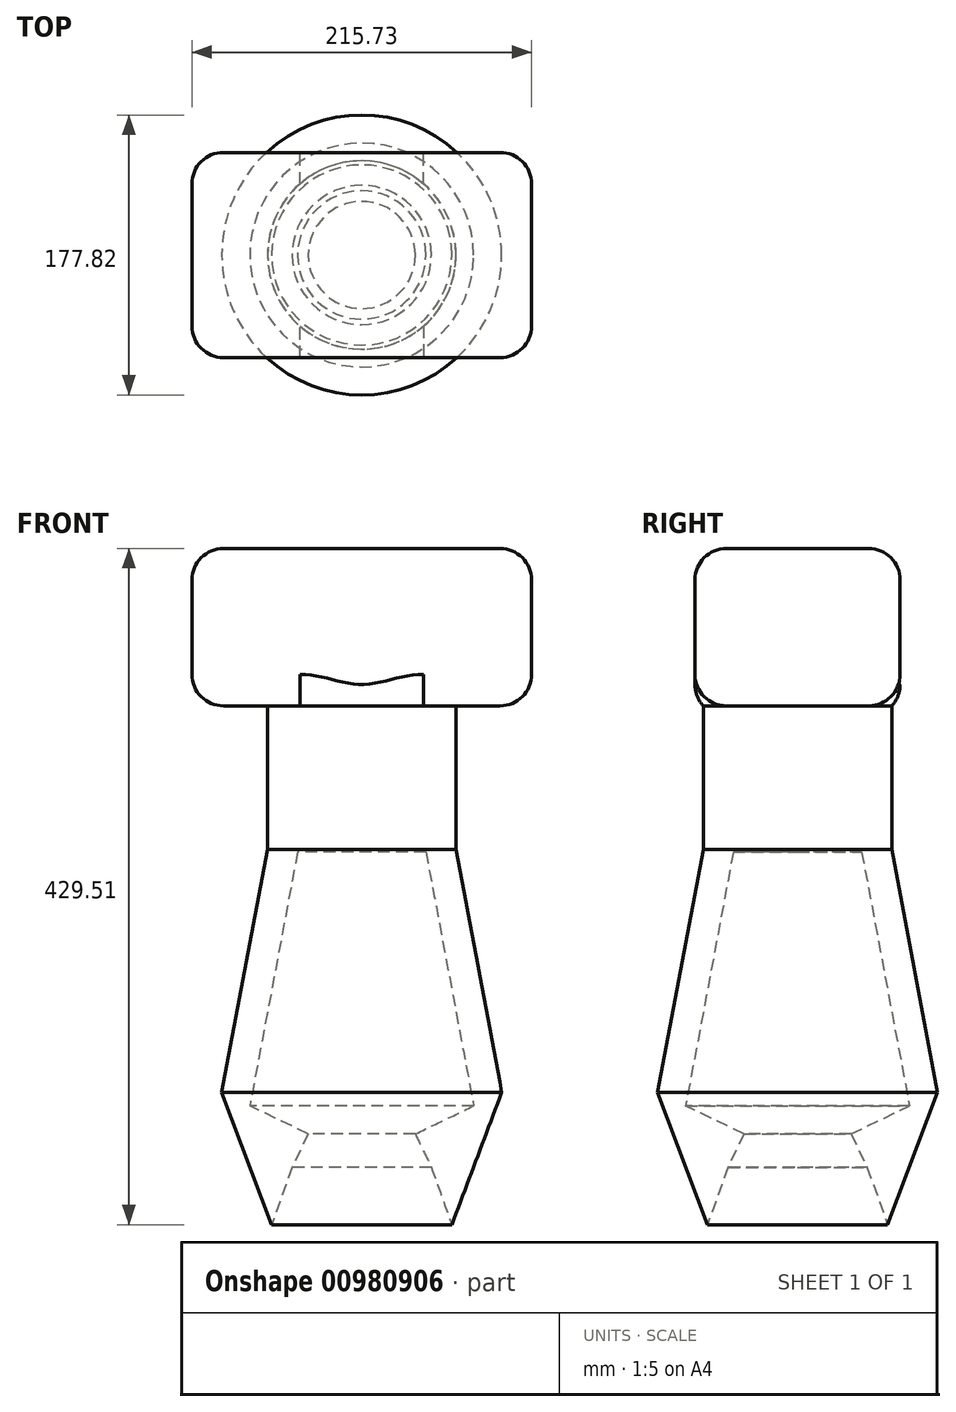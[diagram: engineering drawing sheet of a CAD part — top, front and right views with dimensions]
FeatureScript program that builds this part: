
annotation { "Feature Type Name" : "Feature", "Feature Type Description" : "" }
export const myFeature = defineFeature(function(context is Context, id is Id, definition is map)
    precondition{}
    {
        {
            var Q0;
            Q0=qCreatedBy(makeId("Front.planeOp"),FACE);
            var sketch = newSketch(context, id + "F0", { "sketchPlane" : qUnion([Q0])});
            skLineSegment(sketch, "E0", {"start": v(-398.48, 108.19) * mm, "end": v(-398.48, -266.65) * mm});
            skLineSegment(sketch, "E1.bottom", {"start": v(-312.62, 21.55) * mm, "end": v(-484.34, 21.55) * mm});
            skLineSegment(sketch, "E1.top", {"start": v(-312.62, 194.83) * mm, "end": v(-484.34, 194.83) * mm});
            skLineSegment(sketch, "E1.left", {"start": v(-312.62, 21.55) * mm, "end": v(-312.62, 194.83) * mm});
            skLineSegment(sketch, "E1.right", {"start": v(-484.34, 21.55) * mm, "end": v(-484.34, 194.83) * mm});
            skPoint(sketch, "E1.middle", {"position": v(-398.48, 108.19) * mm});
            skLineSegment(sketch, "E2", {"start": v(-439.22, 21.55) * mm, "end": v(-439.22, -71.24) * mm});
            skLineSegment(sketch, "E3", {"start": v(-439.22, -71.24) * mm, "end": v(-398.48, -71.24) * mm});
            skPoint(sketch, "E3.endSnap0", {"position": v(-398.48, -79.23) * mm});
            skLineSegment(sketch, "E4", {"start": v(-439.22, -71.24) * mm, "end": v(-469.57, -232.52) * mm});
            skLineSegment(sketch, "E5", {"start": v(-469.57, -232.52) * mm, "end": v(-398.48, -266.65) * mm});
            skLineSegment(sketch, "E6.MirrorCS", {"start": v(-357.74, 21.55) * mm, "end": v(-357.74, -71.24) * mm});
            skLineSegment(sketch, "E7.MirrorCS", {"start": v(-357.74, -71.24) * mm, "end": v(-398.48, -71.24) * mm});
            skLineSegment(sketch, "E8.MirrorCS", {"start": v(-357.74, -71.24) * mm, "end": v(-327.4, -232.52) * mm});
            skLineSegment(sketch, "E9.MirrorCS", {"start": v(-327.4, -232.52) * mm, "end": v(-398.48, -266.65) * mm});
            skLineSegment(sketch, "E10", {"start": v(-458.3, 21.55) * mm, "end": v(-458.3, -69.5) * mm});
            skLineSegment(sketch, "E11", {"start": v(-458.3, -69.5) * mm, "end": v(-487.4, -224.1) * mm});
            skLineSegment(sketch, "E12", {"start": v(-487.4, -224.1) * mm, "end": v(-455.7, -307.96) * mm});
            skLineSegment(sketch, "E13", {"start": v(-455.7, -307.96) * mm, "end": v(-442.7, -271.54) * mm});
            skLineSegment(sketch, "E14", {"start": v(-442.7, -271.54) * mm, "end": v(-432.5, -250.32) * mm});
            skLineSegment(sketch, "E15.MirrorCS", {"start": v(-338.67, -69.5) * mm, "end": v(-309.58, -224.1) * mm});
            skLineSegment(sketch, "E16.MirrorCS", {"start": v(-338.67, 21.55) * mm, "end": v(-338.67, -69.5) * mm});
            skLineSegment(sketch, "E17.MirrorCS", {"start": v(-309.58, -224.1) * mm, "end": v(-341.27, -307.96) * mm});
            skLineSegment(sketch, "E18.MirrorCS", {"start": v(-341.27, -307.96) * mm, "end": v(-354.27, -271.54) * mm});
            skLineSegment(sketch, "E19.MirrorCS", {"start": v(-354.27, -271.54) * mm, "end": v(-364.46, -250.32) * mm});
            skSolve(sketch);
        }
        {
            var Q0;
            {var subQ4=sQuery(id+"F0.wireOp",EDGE,"E2");Q0=makeQuery(id+"F0.imprint","IMPRINT",FACE,{"disambiguationData":[TD([[makeQuery(id+"F0.imprint","IMPRINT",EDGE,{"derivedFrom":subQ4}),1.0]])]});}
            var Q1;
            {var subQ3=sQuery(id+"F0.wireOp",EDGE,"E2");Q1=makeQuery(id+"F0.imprint","IMPRINT",FACE,{"disambiguationData":[TD([[makeQuery(id+"F0.imprint","IMPRINT",EDGE,{"derivedFrom":subQ3}),-1.0]])]});}
            var Q2;
            Q2=sQuery(id+"F0.wireOp",EDGE,"E0");
            revolve(context, id + "F1", {"surfaceOperationType" : NewSurfaceOperationType.NEW, "entities" : qUnion([Q0, Q1]), "axis" : qUnion([Q2]), "revolveType" : RevolveType.FULL});
        }
        {
            var Q0;
            Q0=makeQuery(id+"F1.opRevolve","SWEPT_FACE",FACE,{"disambiguationData":[OSD([sQuery(id+"F0.wireOp",EDGE,"E1.bottom")])]});
            var sketch = newSketch(context, id + "F2", { "sketchPlane" : qUnion([Q0])});
            skLineSegment(sketch, "E20.bottom", {"start": v(-290.62, -65.15) * mm, "end": v(-506.35, -65.15) * mm});
            skLineSegment(sketch, "E20.top", {"start": v(-290.62, 65.15) * mm, "end": v(-506.35, 65.15) * mm});
            skLineSegment(sketch, "E20.left", {"start": v(-290.62, -65.15) * mm, "end": v(-290.62, 65.15) * mm});
            skLineSegment(sketch, "E20.right", {"start": v(-506.35, -65.15) * mm, "end": v(-506.35, 65.15) * mm});
            skPoint(sketch, "E20.middle", {"position": v(-398.48, 0) * mm});
            skLineSegment(sketch, "E21", {"start": v(-454.64, 65.15) * mm, "end": v(-454.64, -65.15) * mm});
            skLineSegment(sketch, "E22", {"start": v(-398.48, 65.15) * mm, "end": v(-398.48, -65.15) * mm});
            skLineSegment(sketch, "E23.MirrorCS", {"start": v(-342.33, 65.15) * mm, "end": v(-342.33, -65.15) * mm});
            skSolve(sketch);
        }
        {
            var Q0;
            {var subQ0=sQuery(id+"F2.wireOp",EDGE,"E21");var subQ1=makeQuery(id+"F1.opRevolve","SWEPT_EDGE",EDGE,{"disambiguationData":[OSD([sQuery(id+"F0.wireOp",EDGE,"E1.bottom"),sQuery(id+"F0.wireOp",EDGE,"E10")])]});var subQ2=makeQuery(id+"F2.imprint","INTERSECT",VERTEX,{"disambiguationData":[OD(0.0)],"derivedFrom":[subQ1,subQ0]});Q0=makeQuery(id+"F2.imprint","IMPRINT",FACE,{"disambiguationData":[TD([[makeQuery(id+"F2.imprint","IMPRINT",EDGE,{"disambiguationData":[TD([[subQ2,-1.0]])],"derivedFrom":subQ0}),-1.0]])]});}
            var Q1;
            {var subQ0=sQuery(id+"F2.wireOp",EDGE,"E23.MirrorCS");var subQ1=makeQuery(id+"F1.opRevolve","SWEPT_EDGE",EDGE,{"disambiguationData":[OSD([sQuery(id+"F0.wireOp",EDGE,"E1.bottom"),sQuery(id+"F0.wireOp",EDGE,"E10")])]});var subQ2=makeQuery(id+"F2.imprint","INTERSECT",VERTEX,{"disambiguationData":[OD(0.0)],"derivedFrom":[subQ1,subQ0]});Q1=makeQuery(id+"F2.imprint","IMPRINT",FACE,{"disambiguationData":[TD([[makeQuery(id+"F2.imprint","IMPRINT",EDGE,{"disambiguationData":[TD([[subQ2,-1.0]])],"derivedFrom":subQ0}),1.0]])]});}
            var Q2;
            {var subQ5=sQuery(id+"F2.wireOp",EDGE,"E20.left");Q2=makeQuery(id+"F2.imprint","IMPRINT",FACE,{"disambiguationData":[TD([[makeQuery(id+"F2.imprint","IMPRINT",EDGE,{"derivedFrom":subQ5}),1.0]])]});}
            var Q3;
            {var subQ0=sQuery(id+"F2.wireOp",EDGE,"E22");var subQ1=makeQuery(id+"F1.opRevolve","SWEPT_EDGE",EDGE,{"disambiguationData":[OSD([sQuery(id+"F0.wireOp",EDGE,"E1.bottom"),sQuery(id+"F0.wireOp",EDGE,"E10")])]});var subQ2=makeQuery(id+"F2.imprint","INTERSECT",VERTEX,{"disambiguationData":[OD(0.0)],"derivedFrom":[subQ1,subQ0]});Q3=makeQuery(id+"F2.imprint","IMPRINT",FACE,{"disambiguationData":[TD([[makeQuery(id+"F2.imprint","IMPRINT",EDGE,{"disambiguationData":[TD([[subQ2,-1.0]])],"derivedFrom":subQ0}),1.0]])]});}
            var Q4;
            {var subQ0=sQuery(id+"F2.wireOp",EDGE,"E22");var subQ1=sQuery(id+"F2.wireOp",EDGE,"E20.top");var subQ2=makeQuery(id+"F2.imprint","INTERSECT",VERTEX,{"derivedFrom":[subQ1,subQ0]});Q4=makeQuery(id+"F2.imprint","IMPRINT",FACE,{"disambiguationData":[TD([[makeQuery(id+"F2.imprint","IMPRINT",EDGE,{"disambiguationData":[TD([[subQ2,1.0]])],"derivedFrom":subQ1}),1.0]])]});}
            var Q5;
            {var subQ0=sQuery(id+"F2.wireOp",EDGE,"E22");var subQ1=sQuery(id+"F2.wireOp",EDGE,"E20.bottom");var subQ2=makeQuery(id+"F2.imprint","INTERSECT",VERTEX,{"derivedFrom":[subQ1,subQ0]});Q5=makeQuery(id+"F2.imprint","IMPRINT",FACE,{"disambiguationData":[TD([[makeQuery(id+"F2.imprint","IMPRINT",EDGE,{"disambiguationData":[TD([[subQ2,1.0]])],"derivedFrom":subQ1}),-1.0]])]});}
            var Q6;
            {var subQ0=sQuery(id+"F2.wireOp",EDGE,"E21");var subQ1=sQuery(id+"F2.wireOp",EDGE,"E20.bottom");var subQ2=makeQuery(id+"F2.imprint","INTERSECT",VERTEX,{"derivedFrom":[subQ1,subQ0]});Q6=makeQuery(id+"F2.imprint","IMPRINT",FACE,{"disambiguationData":[TD([[makeQuery(id+"F2.imprint","IMPRINT",EDGE,{"disambiguationData":[TD([[subQ2,1.0]])],"derivedFrom":subQ1}),-1.0]])]});}
            var Q7;
            {var subQ5=sQuery(id+"F2.wireOp",EDGE,"E20.right");Q7=makeQuery(id+"F2.imprint","IMPRINT",FACE,{"disambiguationData":[TD([[makeQuery(id+"F2.imprint","IMPRINT",EDGE,{"derivedFrom":subQ5}),-1.0]])]});}
            var Q8;
            {var subQ0=sQuery(id+"F2.wireOp",EDGE,"E21");var subQ1=sQuery(id+"F2.wireOp",EDGE,"E20.top");var subQ2=makeQuery(id+"F2.imprint","INTERSECT",VERTEX,{"derivedFrom":[subQ1,subQ0]});Q8=makeQuery(id+"F2.imprint","IMPRINT",FACE,{"disambiguationData":[TD([[makeQuery(id+"F2.imprint","IMPRINT",EDGE,{"disambiguationData":[TD([[subQ2,1.0]])],"derivedFrom":subQ1}),1.0]])]});}
            var Q9;
            {var subQ0=sQuery(id+"F2.wireOp",EDGE,"E21");var subQ1=makeQuery(id+"F1.opRevolve","SWEPT_EDGE",EDGE,{"disambiguationData":[OSD([sQuery(id+"F0.wireOp",EDGE,"E1.bottom"),sQuery(id+"F0.wireOp",EDGE,"E10")])]});var subQ2=makeQuery(id+"F2.imprint","INTERSECT",VERTEX,{"disambiguationData":[OD(0.0)],"derivedFrom":[subQ1,subQ0]});Q9=makeQuery(id+"F2.imprint","IMPRINT",FACE,{"disambiguationData":[TD([[makeQuery(id+"F2.imprint","IMPRINT",EDGE,{"disambiguationData":[TD([[subQ2,-1.0]])],"derivedFrom":subQ0}),1.0]])]});}
            extrude(context, id + "F3", {"entities" : qUnion([Q0, Q1, Q2, Q3, Q4, Q5, Q6, Q7, Q8, Q9]), "operationType" : NewBodyOperationType.ADD, "depth" : 100 * mm, "offsetDistance" : 25 * mm});
        }
        {
            var Q0;
            Q0=makeQuery(id+"F3.opExtrude","CAP_EDGE",EDGE,{"disambiguationData":[OSD([sQuery(id+"F2.wireOp",EDGE,"E20.right")])],"isStart":false});
            var Q1;
            Q1=makeQuery(id+"F3.opExtrude","CAP_EDGE",EDGE,{"disambiguationData":[OSD([sQuery(id+"F2.wireOp",EDGE,"E20.left")])],"isStart":false});
            var Q2;
            Q2=makeQuery(id+"F3.opExtrude","CAP_EDGE",EDGE,{"disambiguationData":[OSD([sQuery(id+"F2.wireOp",EDGE,"E20.top")])],"isStart":false});
            var Q3;
            Q3=makeQuery(id+"F3.opExtrude","CAP_EDGE",EDGE,{"disambiguationData":[OSD([sQuery(id+"F2.wireOp",EDGE,"E20.bottom")])],"isStart":false});
            var Q4;
            Q4=makeQuery(id+"F3.opExtrude","SWEPT_EDGE",EDGE,{"disambiguationData":[OSD([sQuery(id+"F2.wireOp",EDGE,"E20.bottom"),sQuery(id+"F2.wireOp",EDGE,"E20.right")])]});
            var Q5;
            Q5=makeQuery(id+"F3.opExtrude","CAP_EDGE",EDGE,{"disambiguationData":[OSD([sQuery(id+"F2.wireOp",EDGE,"E20.right")])],"isStart":true});
            var Q6;
            Q6=makeQuery(id+"F3.opExtrude","CAP_EDGE",EDGE,{"disambiguationData":[OSD([sQuery(id+"F2.wireOp",EDGE,"E20.bottom")])],"isStart":true});
            var Q7;
            Q7=makeQuery(id+"F3.opExtrude","SWEPT_EDGE",EDGE,{"disambiguationData":[OSD([sQuery(id+"F2.wireOp",EDGE,"E20.top"),sQuery(id+"F2.wireOp",EDGE,"E20.right")])]});
            var Q8;
            Q8=makeQuery(id+"F3.opExtrude","SWEPT_FACE",FACE,{"disambiguationData":[OSD([sQuery(id+"F2.wireOp",EDGE,"E20.top")])]});
            var Q9;
            Q9=makeQuery(id+"F3.opExtrude","CAP_EDGE",EDGE,{"disambiguationData":[OSD([sQuery(id+"F2.wireOp",EDGE,"E20.left")])],"isStart":true});
            var Q10;
            Q10=makeQuery(id+"F3.opExtrude","SWEPT_EDGE",EDGE,{"disambiguationData":[OSD([sQuery(id+"F2.wireOp",EDGE,"E20.bottom"),sQuery(id+"F2.wireOp",EDGE,"E20.left")])]});
            fillet(context, id + "F4", {"entities" : qUnion([Q0, Q1, Q2, Q3, Q4, Q5, Q6, Q7, Q8, Q9, Q10]), "radius" : 20 * mm, "tangentPropagation" : true, "allowEdgeOverflow" : false});
        }
    });
